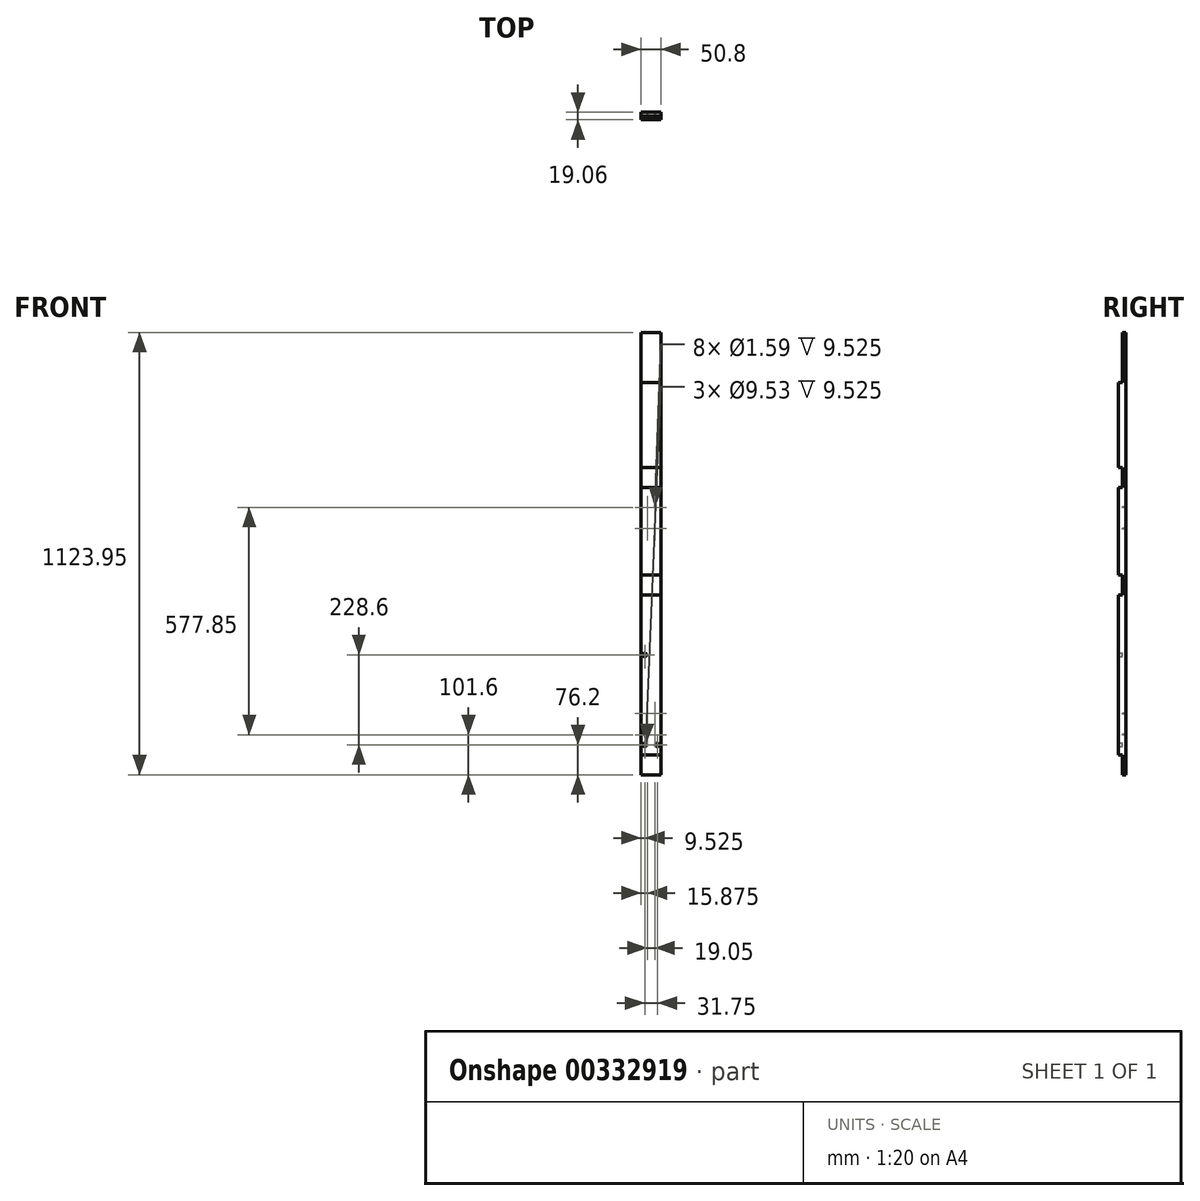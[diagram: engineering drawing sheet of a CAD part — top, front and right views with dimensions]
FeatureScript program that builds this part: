
annotation { "Feature Type Name" : "Feature", "Feature Type Description" : "" }
export const myFeature = defineFeature(function(context is Context, id is Id, definition is map)
    precondition{}
    {
        {
            var Q0;
            Q0=qCreatedBy(makeId("Top.planeOp"),FACE);
            var sketch = newSketch(context, id + "F0", { "sketchPlane" : qUnion([Q0])});
            skLineSegment(sketch, "E0.bottom", {"start": v(25.4, 9.53) * mm, "end": v(-25.4, 9.53) * mm});
            skLineSegment(sketch, "E0.top", {"start": v(25.4, -9.53) * mm, "end": v(-25.4, -9.53) * mm});
            skLineSegment(sketch, "E0.left", {"start": v(25.4, 9.53) * mm, "end": v(25.4, -9.52) * mm});
            skLineSegment(sketch, "E0.right", {"start": v(-25.4, 9.53) * mm, "end": v(-25.4, -9.53) * mm});
            skPoint(sketch, "E0.middle", {"position": v(0, 0) * mm});
            skSolve(sketch);
        }
        {
            var Q0;
            Q0=makeQuery(id+"F0.imprint","IMPRINT",FACE,{"disambiguationData":[TD([[makeQuery(id+"F0.imprint","IMPRINT",EDGE,{"derivedFrom":sQuery(id+"F0.wireOp",EDGE,"E0.bottom")}),1.0]])]});
            extrude(context, id + "F1", {"entities" : qUnion([Q0]), "depth" : 1123.95 * mm});
        }
        {
            var Q0;
            Q0=qCreatedBy(makeId("Front.planeOp"),FACE);
            var sketch = newSketch(context, id + "F2", { "sketchPlane" : qUnion([Q0])});
            skLineSegment(sketch, "E1.bottom", {"start": v(-38.77, 0) * mm, "end": v(83.66, 0) * mm});
            skLineSegment(sketch, "E1.top", {"start": v(-38.77, 50.8) * mm, "end": v(83.66, 50.8) * mm});
            skLineSegment(sketch, "E1.left", {"start": v(-38.77, 0) * mm, "end": v(-38.77, 50.8) * mm});
            skLineSegment(sketch, "E1.right", {"start": v(83.66, 0) * mm, "end": v(83.66, 50.8) * mm});
            skLineSegment(sketch, "E2.bottom", {"start": v(-44.21, 730.25) * mm, "end": v(49.65, 730.25) * mm});
            skLineSegment(sketch, "E2.top", {"start": v(-44.21, 781.05) * mm, "end": v(49.65, 781.05) * mm});
            skLineSegment(sketch, "E2.left", {"start": v(-44.21, 730.25) * mm, "end": v(-44.21, 781.05) * mm});
            skLineSegment(sketch, "E2.right", {"start": v(49.65, 730.25) * mm, "end": v(49.65, 781.05) * mm});
            skLineSegment(sketch, "E3.bottom", {"start": v(-74.14, 508) * mm, "end": v(71.42, 508) * mm});
            skLineSegment(sketch, "E3.top", {"start": v(-74.14, 457.2) * mm, "end": v(71.42, 457.2) * mm});
            skLineSegment(sketch, "E3.left", {"start": v(-74.14, 508) * mm, "end": v(-74.14, 457.2) * mm});
            skLineSegment(sketch, "E3.right", {"start": v(71.42, 508) * mm, "end": v(71.42, 457.2) * mm});
            skLineSegment(sketch, "E4.bottom", {"start": v(-210.36, 996.95) * mm, "end": v(132.8, 996.95) * mm});
            skLineSegment(sketch, "E4.top", {"start": v(-210.36, 1123.95) * mm, "end": v(132.8, 1123.95) * mm});
            skLineSegment(sketch, "E4.left", {"start": v(-210.36, 996.95) * mm, "end": v(-210.36, 1123.95) * mm});
            skLineSegment(sketch, "E4.right", {"start": v(132.8, 996.95) * mm, "end": v(132.8, 1123.95) * mm});
            skSolve(sketch);
        }
        {
            var Q0;
            Q0=qSketchRegion(id+"F2",true);
            extrude(context, id + "F3", {"entities" : qUnion([Q0]), "operationType" : NewBodyOperationType.REMOVE, "depth" : 25.4 * mm});
        }
        {
            var Q0;
            Q0=qCreatedBy(makeId("Front.planeOp"),FACE);
            var sketch = newSketch(context, id + "F4", { "sketchPlane" : qUnion([Q0])});
            skCircle(sketch, "E5", {"center": v(9.52, 101.6) * mm, "radius": 0.8 * mm});
            skCircle(sketch, "E6", {"center": v(9.52, 155.58) * mm, "radius": 0.8 * mm});
            skCircle(sketch, "E7", {"center": v(9.52, 625.48) * mm, "radius": 0.8 * mm});
            skCircle(sketch, "E8", {"center": v(9.52, 679.45) * mm, "radius": 0.8 * mm});
            skLineSegment(sketch, "E9", {"start": v(0, 0) * mm, "end": v(0, 1192.46) * mm, "construction": true});
            skLineSegment(sketch, "E10.bottom", {"start": v(9.52, 101.6) * mm, "end": v(-9.52, 101.6) * mm, "construction": true});
            skLineSegment(sketch, "E10.top", {"start": v(9.52, 679.45) * mm, "end": v(-9.53, 679.45) * mm, "construction": true});
            skLineSegment(sketch, "E10.left", {"start": v(9.53, 101.6) * mm, "end": v(9.52, 679.45) * mm, "construction": true});
            skLineSegment(sketch, "E10.right", {"start": v(-9.52, 101.6) * mm, "end": v(-9.53, 679.45) * mm, "construction": true});
            skCircle(sketch, "E11", {"center": v(-9.53, 625.48) * mm, "radius": 0.8 * mm});
            skCircle(sketch, "E12", {"center": v(-9.53, 679.45) * mm, "radius": 0.8 * mm});
            skCircle(sketch, "E13", {"center": v(-9.52, 101.6) * mm, "radius": 0.8 * mm});
            skCircle(sketch, "E14", {"center": v(-9.52, 155.58) * mm, "radius": 0.8 * mm});
            skSolve(sketch);
        }
        {
            var Q0;
            Q0=qSketchRegion(id+"F4",true);
            extrude(context, id + "F5", {"entities" : qUnion([Q0]), "operationType" : NewBodyOperationType.REMOVE, "oppositeDirection" : true, "depth" : 25.4 * mm});
        }
        {
            var Q0;
            Q0=qCreatedBy(makeId("Front.planeOp"),FACE);
            var sketch = newSketch(context, id + "F6", { "sketchPlane" : qUnion([Q0])});
            skCircle(sketch, "E15", {"center": v(15.88, 76.2) * mm, "radius": 4.76 * mm});
            skCircle(sketch, "E16", {"center": v(-15.88, 76.2) * mm, "radius": 4.76 * mm});
            skCircle(sketch, "E17", {"center": v(-15.88, 304.8) * mm, "radius": 4.76 * mm});
            skSolve(sketch);
        }
        {
            var Q0;
            Q0=qSketchRegion(id+"F6",true);
            extrude(context, id + "F7", {"entities" : qUnion([Q0]), "operationType" : NewBodyOperationType.REMOVE, "depth" : 25.4 * mm});
        }
    });
